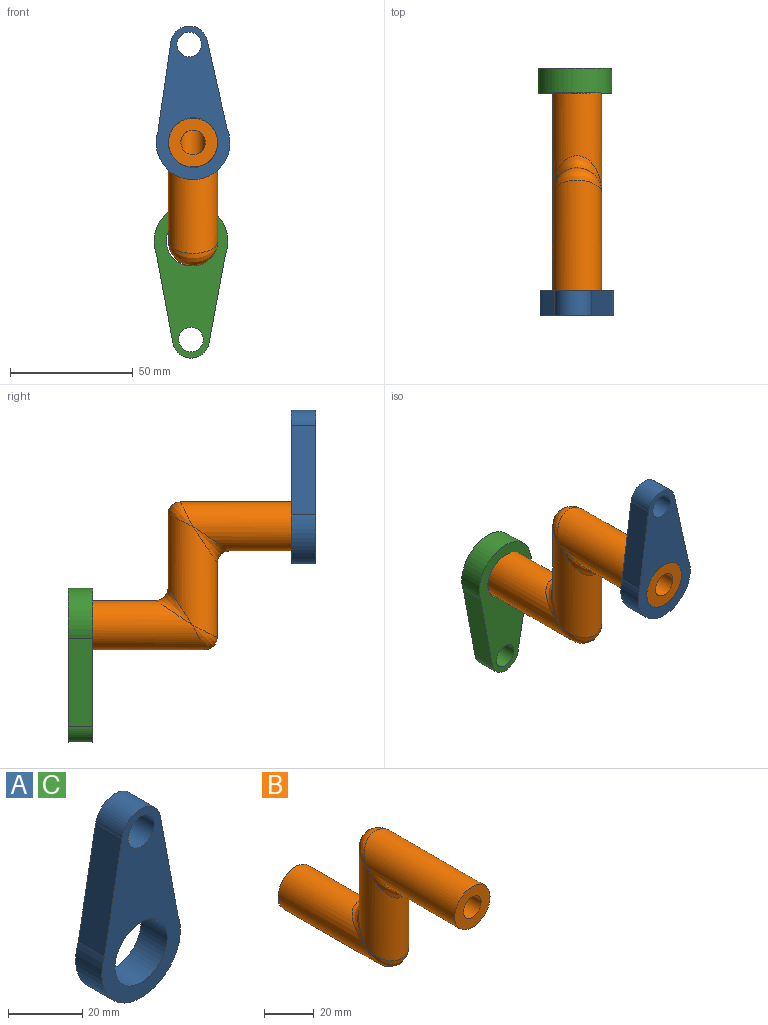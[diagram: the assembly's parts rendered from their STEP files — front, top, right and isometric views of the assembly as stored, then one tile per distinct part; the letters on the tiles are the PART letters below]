
ASSEMBLY  parts=3 mates=3
PART A: 8 faces, bbox 30x10x62.5 mm
  f0: cylinder r=15mm len=30mm, axis (0,1,0), area 580.6mm2, adj f1,f4,f6,f7
  f1: plane 36.01x10mm, normal (0.98,0,0.18), area 366.2mm2, adj f0,f2,f6,f7
  f2: cylinder r=7.5mm len=14.75mm, axis (0,1,0), area 208.3mm2, adj f1,f4,f6,f7
  f3: cylinder r=5mm len=10mm, axis (0,1,0), area 314.2mm2, adj f6,f7
  f4: plane 36.01x10mm, normal (-0.98,0,0.18), area 366.2mm2, adj f0,f2,f6,f7
  f5: cylinder r=10mm len=20mm, axis (0,1,0), area 628.3mm2, adj f6,f7
  f6: plane 62.5x30mm, normal (0,-1,0), area 956.1mm2, adj f0,f1,f2,f3,f4,f5
  f7: plane 62.5x30mm, normal (0,1,0), area 956.1mm2, adj f0,f1,f2,f3,f4,f5
PART B: 12 faces, bbox 20x100x60.2 mm
  f0: cylinder r=5mm len=55mm, axis (0,-1,0), area 1570.8mm2, adj f1,f3
  f1: cylinder r=5mm len=50.16mm, axis (0,0,1), area 1261.5mm2, adj f0,f2
  f2: cylinder r=5mm len=55mm, axis (0,-1,0), area 1570.8mm2, adj f1,f4
  f3: plane 20x20mm, normal (0,-1,0), area 235.6mm2, adj f0,f5
  f4: plane 20x20mm, normal (0,1,0), area 235.6mm2, adj f2,f7
  f5: cylinder r=10mm len=55.02mm, axis (0,-1,0), area 2941.6mm2, adj f3,f8,f9
  f6: cylinder r=10mm len=50.19mm, axis (0,0,1), area 2122.9mm2, adj f8,f9,f10,f11
  f7: cylinder r=10mm len=55mm, axis (0,-1,0), area 2920.1mm2, adj f4,f10,f11
  f8: bspline ~20x15mm, area 180.9mm2, adj f5,f6
  f9: bspline ~20x10mm, area 165mm2, adj f5,f6
  f10: bspline ~20x15mm, area 180.9mm2, adj f6,f7
  f11: bspline ~20x10mm, area 165mm2, adj f6,f7
PART C: same geometry as A
PLACE A rot(axis=(0,-1,0),2.2deg) t=(-1.54,20.08,74.98)mm
PLACE B t=(-1.54,115.08,34.98)mm
PLACE C rot(axis=(0,1,0),180deg) t=(-2.38,110.62,34.95)mm
MATE parallel A.f5 <-> B.f0  axis (0,-1,0) through (-1.54,15.08,74.98)mm
MATE parallel C.f5 <-> B.f7  axis (0,1,0) through (-2.38,115.62,34.95)mm
MATE parallel A.f6 <-> C.f7  axis (0,-1,0) through (8.24,15.08,98.74)mm
